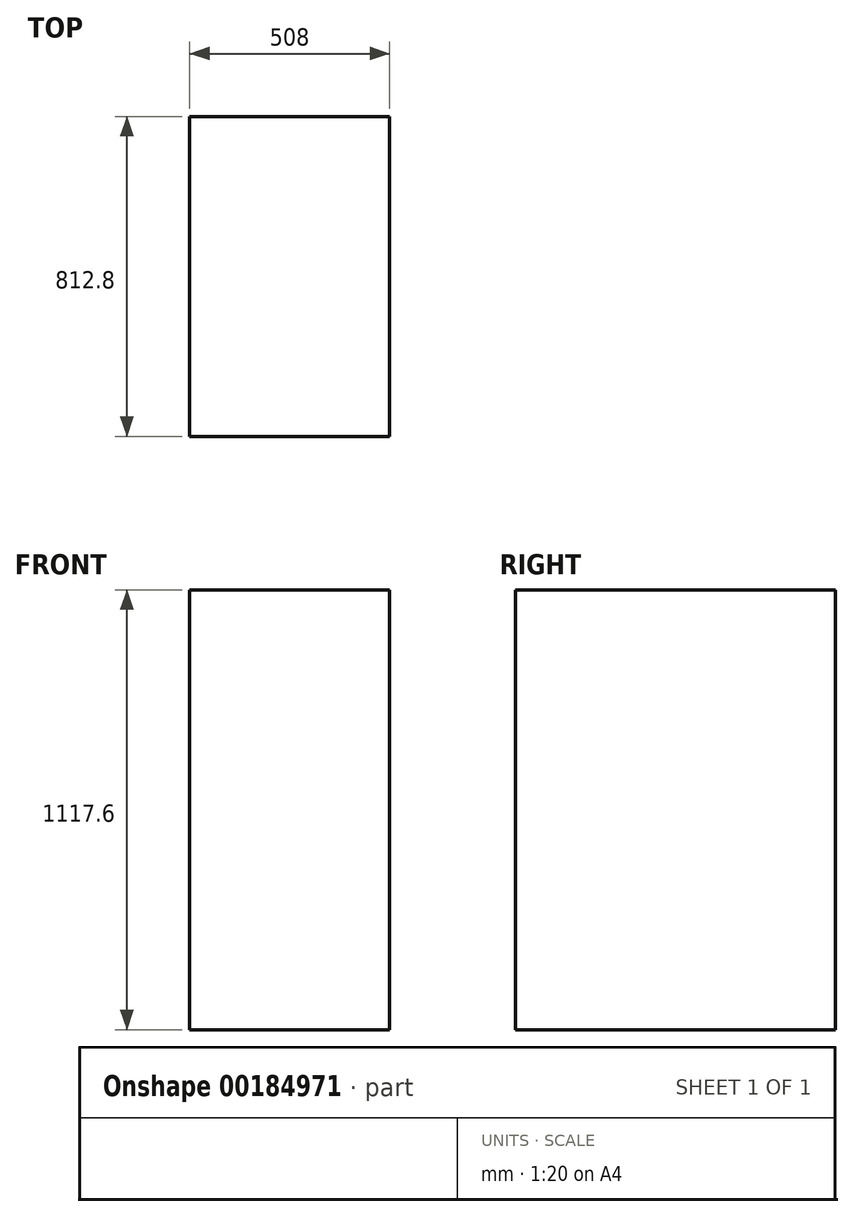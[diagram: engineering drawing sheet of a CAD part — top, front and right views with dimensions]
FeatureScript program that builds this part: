
annotation { "Feature Type Name" : "Feature", "Feature Type Description" : "" }
export const myFeature = defineFeature(function(context is Context, id is Id, definition is map)
    precondition{}
    {
        {
            var Q0;
            Q0=qCreatedBy(makeId("Top.planeOp"),FACE);
            var sketch = newSketch(context, id + "F0", { "sketchPlane" : qUnion([Q0])});
            skLineSegment(sketch, "E0.bottom", {"start": v(254, 406.4) * mm, "end": v(-254, 406.4) * mm});
            skLineSegment(sketch, "E0.top", {"start": v(254, -406.4) * mm, "end": v(-254, -406.4) * mm});
            skLineSegment(sketch, "E0.left", {"start": v(254, 406.4) * mm, "end": v(254, -406.4) * mm});
            skLineSegment(sketch, "E0.right", {"start": v(-254, 406.4) * mm, "end": v(-254, -406.4) * mm});
            skPoint(sketch, "E0.middle", {"position": v(0, 0) * mm});
            skSolve(sketch);
        }
        {
            var Q0;
            Q0=makeQuery(id+"F0.imprint","IMPRINT",FACE,{"disambiguationData":[TD([[makeQuery(id+"F0.imprint","IMPRINT",EDGE,{"derivedFrom":sQuery(id+"F0.wireOp",EDGE,"E0.bottom")}),1.0]])]});
            extrude(context, id + "F1", {"entities" : qUnion([Q0]), "depth" : 1117.6 * mm});
        }
    });
